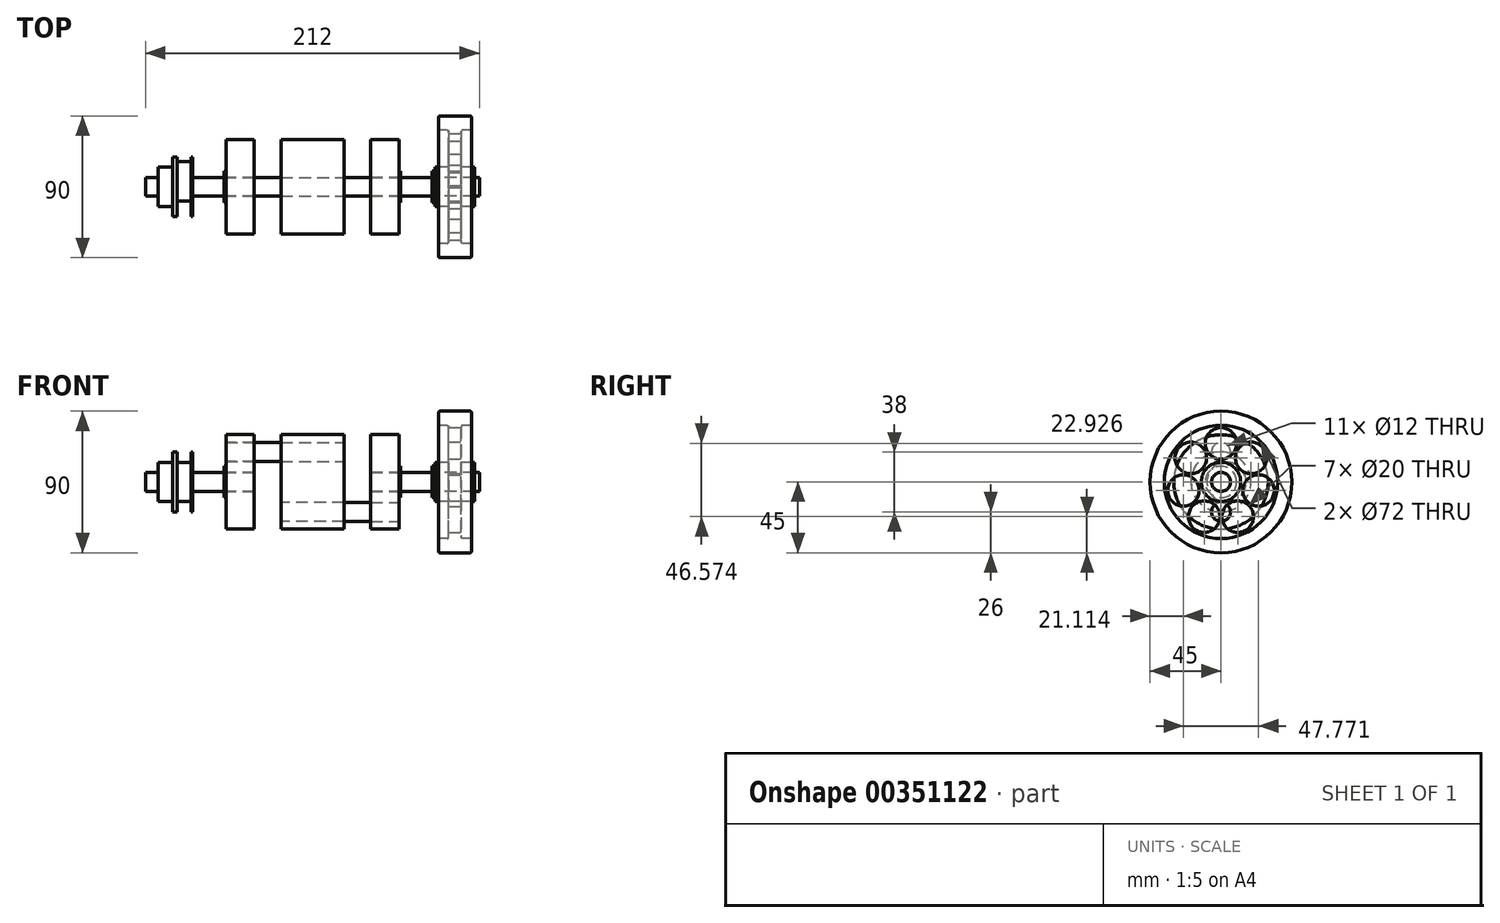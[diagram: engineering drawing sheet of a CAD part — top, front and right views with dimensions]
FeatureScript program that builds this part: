
annotation { "Feature Type Name" : "Feature", "Feature Type Description" : "" }
export const myFeature = defineFeature(function(context is Context, id is Id, definition is map)
    precondition{}
    {
        {
            var Q0;
            Q0=qCreatedBy(makeId("Right.planeOp"),FACE);
            var sketch = newSketch(context, id + "F0", { "sketchPlane" : qUnion([Q0])});
            skCircle(sketch, "E0", {"center": v(0, 0) * mm, "radius": 30 * mm});
            skCircle(sketch, "E1", {"center": v(0, 19) * mm, "radius": 6 * mm});
            skCircle(sketch, "E2", {"center": v(0, -19) * mm, "radius": 6 * mm});
            skSolve(sketch);
        }
        {
            var Q0;
            Q0=makeQuery(id+"F0.imprint","IMPRINT",FACE,{"disambiguationData":[TD([[makeQuery(id+"F0.imprint","IMPRINT",EDGE,{"derivedFrom":sQuery(id+"F0.wireOp",EDGE,"E0")}),1.0]])]});
            extrude(context, id + "F1", {"entities" : qUnion([Q0]), "endBound" : BoundingType.SYMMETRIC, "depth" : 40 * mm});
        }
        {
            var Q0;
            Q0=makeQuery(id+"F0.imprint","IMPRINT",FACE,{"disambiguationData":[TD([[makeQuery(id+"F0.imprint","IMPRINT",EDGE,{"derivedFrom":sQuery(id+"F0.wireOp",EDGE,"E1")}),1.0]])]});
            extrude(context, id + "F2", {"entities" : qUnion([Q0]), "oppositeDirection" : true, "depth" : 55 * mm, "hasSecondDirection" : true, "secondDirectionOppositeDirection" : false, "secondDirectionDepth" : 20 * mm});
        }
        {
            var Q0;
            Q0=makeQuery(id+"F0.imprint","IMPRINT",FACE,{"disambiguationData":[TD([[makeQuery(id+"F0.imprint","IMPRINT",EDGE,{"derivedFrom":sQuery(id+"F0.wireOp",EDGE,"E2")}),1.0]])]});
            extrude(context, id + "F3", {"entities" : qUnion([Q0]), "depth" : 55 * mm, "hasSecondDirection" : true, "secondDirectionOppositeDirection" : true, "secondDirectionDepth" : 20 * mm});
        }
        {
            var Q0;
            Q0=makeQuery(id+"F3.opExtrude","CAP_FACE",FACE,{"disambiguationData":[OSD([sQuery(id+"F0.wireOp",EDGE,"E2")])],"isStart":false});
            var sketch = newSketch(context, id + "F4", { "sketchPlane" : qUnion([Q0])});
            skCircle(sketch, "E3", {"center": v(0, 0) * mm, "radius": 30 * mm});
            skCircle(sketch, "E4", {"center": v(0, 0) * mm, "radius": 6 * mm});
            skCircle(sketch, "E5", {"center": v(0, 0) * mm, "radius": 10 * mm});
            skSolve(sketch);
        }
        {
            var Q0;
            Q0=makeQuery(id+"F4.imprint","IMPRINT",FACE,{"disambiguationData":[TD([[makeQuery(id+"F4.imprint","IMPRINT",EDGE,{"derivedFrom":sQuery(id+"F4.wireOp",EDGE,"E3")}),1.0]])]});
            var Q1;
            Q1=makeQuery(id+"F4.imprint","IMPRINT",FACE,{"disambiguationData":[TD([[makeQuery(id+"F4.imprint","IMPRINT",EDGE,{"derivedFrom":sQuery(id+"F4.wireOp",EDGE,"E4")}),-1.0]])]});
            extrude(context, id + "F5", {"entities" : qUnion([Q0, Q1]), "oppositeDirection" : true, "depth" : 18 * mm});
        }
        {
            var Q0;
            Q0=makeQuery(id+"F5.opExtrude","SWEPT_BODY",BODY,{"disambiguationData":[OSD([sQuery(id+"F0.wireOp",EDGE,"E2"),sQuery(id+"F4.wireOp",EDGE,"E3"),sQuery(id+"F4.wireOp",EDGE,"E4")])]});
            var Q1;
            Q1=qCreatedBy(makeId("Right.planeOp"),FACE);
            mirror(context, id + "F6", {"entities" : qUnion([Q0]), "mirrorPlane" : qUnion([Q1])});
        }
        {
            var Q0;
            Q0=makeQuery(id+"F6.opPattern","COPY",BODY,{"derivedFrom":makeQuery(id+"F5.opExtrude","SWEPT_BODY",BODY,{"disambiguationData":[OSD([sQuery(id+"F0.wireOp",EDGE,"E2"),sQuery(id+"F4.wireOp",EDGE,"E3"),sQuery(id+"F4.wireOp",EDGE,"E4")])]}),"instanceName":"1"});
            var Q1;
            Q1=makeQuery(id+"F6.opPattern","COPY",FACE,{"derivedFrom":makeQuery(id+"F5.opExtrude","SWEPT_FACE",FACE,{"disambiguationData":[OSD([sQuery(id+"F4.wireOp",EDGE,"E4")])]}),"instanceName":"1"});
            transform(context, id + "F7", {"entities" : qUnion([Q0]), "transformType" : TransformType.ROTATION, "transformAxis" : qUnion([Q1]), "angle" : 180 * degree, "makeCopy" : false});
        }
        {
            var Q0;
            Q0=makeQuery(id+"F4.imprint","IMPRINT",FACE,{"disambiguationData":[TD([[makeQuery(id+"F4.imprint","IMPRINT",EDGE,{"derivedFrom":sQuery(id+"F4.wireOp",EDGE,"E4")}),1.0]])]});
            extrude(context, id + "F8", {"entities" : qUnion([Q0]), "depth" : 51 * mm, "hasSecondDirection" : true, "secondDirectionOppositeDirection" : true, "secondDirectionDepth" : 18 * mm});
        }
        {
            var Q0;
            Q0=makeQuery(id+"F4.imprint","IMPRINT",FACE,{"disambiguationData":[TD([[makeQuery(id+"F4.imprint","IMPRINT",EDGE,{"derivedFrom":sQuery(id+"F4.wireOp",EDGE,"E4")}),-1.0]])]});
            extrude(context, id + "F9", {"entities" : qUnion([Q0]), "depth" : 1 * mm});
        }
        {
            var Q0;
            Q0=makeQuery(id+"F8.opExtrude","SWEPT_BODY",BODY,{"disambiguationData":[OSD([sQuery(id+"F4.wireOp",EDGE,"E4")])]});
            var Q1;
            Q1=makeQuery(id+"F9.opExtrude","SWEPT_BODY",BODY,{"disambiguationData":[OSD([sQuery(id+"F4.wireOp",EDGE,"E4"),sQuery(id+"F4.wireOp",EDGE,"E5")])]});
            var Q2;
            Q2=qCreatedBy(makeId("Right.planeOp"),FACE);
            mirror(context, id + "F10", {"entities" : qUnion([Q0, Q1]), "mirrorPlane" : qUnion([Q2])});
        }
        {
            var Q0;
            Q0=qCreatedBy(makeId("Front.planeOp"),FACE);
            var sketch = newSketch(context, id + "F11", { "sketchPlane" : qUnion([Q0])});
            skLineSegment(sketch, "E6", {"start": v(0, 0) * mm, "end": v(137.97, 0) * mm, "construction": true});
            skLineSegment(sketch, "E7", {"start": v(90.5, 52.84) * mm, "end": v(90.5, -56.17) * mm, "construction": true});
            skLineSegment(sketch, "E8", {"start": v(78, -6) * mm, "end": v(103, -6) * mm});
            skLineSegment(sketch, "E9", {"start": v(103, -6) * mm, "end": v(103, -12.5) * mm});
            skLineSegment(sketch, "E10", {"start": v(103, -12.5) * mm, "end": v(94.5, -12.5) * mm});
            skLineSegment(sketch, "E11", {"start": v(94.5, -12.5) * mm, "end": v(94.5, -36) * mm});
            skLineSegment(sketch, "E12", {"start": v(86.5, -36) * mm, "end": v(86.5, -12.5) * mm});
            skLineSegment(sketch, "E13", {"start": v(86.5, -12.5) * mm, "end": v(78, -12.5) * mm});
            skLineSegment(sketch, "E14", {"start": v(78, -12.5) * mm, "end": v(78, -6) * mm});
            skLineSegment(sketch, "E15", {"start": v(94.5, -36) * mm, "end": v(101, -36) * mm});
            skLineSegment(sketch, "E16", {"start": v(101, -36) * mm, "end": v(101, -45) * mm});
            skLineSegment(sketch, "E17", {"start": v(101, -45) * mm, "end": v(80, -45) * mm});
            skLineSegment(sketch, "E18", {"start": v(80, -45) * mm, "end": v(80, -36) * mm});
            skLineSegment(sketch, "E19", {"start": v(80, -36) * mm, "end": v(86.5, -36) * mm});
            skSolve(sketch);
        }
        {
            var Q0;
            Q0=makeQuery(id+"F11.imprint","IMPRINT",FACE,{"disambiguationData":[TD([[makeQuery(id+"F11.imprint","IMPRINT",EDGE,{"derivedFrom":sQuery(id+"F11.wireOp",EDGE,"E8")}),-1.0]])]});
            var Q1;
            Q1=sQuery(id+"F11.wireOp",EDGE,"E6");
            revolve(context, id + "F12", {"entities" : qUnion([Q0]), "axis" : qUnion([Q1]), "revolveType" : RevolveType.FULL});
        }
        {
            var Q0;
            Q0=makeQuery(id+"F12.opRevolve","SWEPT_FACE",FACE,{"disambiguationData":[OSD([sQuery(id+"F11.wireOp",EDGE,"E11")])]});
            var sketch = newSketch(context, id + "F13", { "sketchPlane" : qUnion([Q0])});
            skLineSegment(sketch, "E20", {"start": v(0, 0) * mm, "end": v(0, 49) * mm, "construction": true});
            skCircle(sketch, "E21", {"center": v(0, 24.5) * mm, "radius": 10 * mm});
            skCircle(sketch, "E22.1.0", {"center": v(19.15, 15.28) * mm, "radius": 10 * mm});
            skCircle(sketch, "E22.2.0", {"center": v(23.89, -5.45) * mm, "radius": 10 * mm});
            skCircle(sketch, "E22.3.0", {"center": v(10.63, -22.07) * mm, "radius": 10 * mm});
            skCircle(sketch, "E22.4.0", {"center": v(-10.63, -22.07) * mm, "radius": 10 * mm});
            skCircle(sketch, "E22.5.0", {"center": v(-23.89, -5.45) * mm, "radius": 10 * mm});
            skCircle(sketch, "E22.6.0", {"center": v(-19.15, 15.28) * mm, "radius": 10 * mm});
            skPoint(sketch, "E22.center", {"position": v(0, 0) * mm});
            skLineSegment(sketch, "E22.anchor1", {"start": v(0, 0) * mm, "end": v(0, 24.5) * mm, "construction": true});
            skLineSegment(sketch, "E22.anchor2", {"start": v(0, 0) * mm, "end": v(-19.15, 15.28) * mm, "construction": true});
            skSolve(sketch);
        }
        {
            var Q0;
            Q0=makeQuery(id+"F13.imprint","IMPRINT",FACE,{"disambiguationData":[TD([[makeQuery(id+"F13.imprint","IMPRINT",EDGE,{"derivedFrom":sQuery(id+"F13.wireOp",EDGE,"E22.4.0")}),1.0]])]});
            var Q1;
            Q1=makeQuery(id+"F13.imprint","IMPRINT",FACE,{"disambiguationData":[TD([[makeQuery(id+"F13.imprint","IMPRINT",EDGE,{"derivedFrom":sQuery(id+"F13.wireOp",EDGE,"E22.3.0")}),1.0]])]});
            var Q2;
            Q2=makeQuery(id+"F13.imprint","IMPRINT",FACE,{"disambiguationData":[TD([[makeQuery(id+"F13.imprint","IMPRINT",EDGE,{"derivedFrom":sQuery(id+"F13.wireOp",EDGE,"E22.2.0")}),1.0]])]});
            var Q3;
            Q3=makeQuery(id+"F13.imprint","IMPRINT",FACE,{"disambiguationData":[TD([[makeQuery(id+"F13.imprint","IMPRINT",EDGE,{"derivedFrom":sQuery(id+"F13.wireOp",EDGE,"E22.1.0")}),1.0]])]});
            var Q4;
            Q4=makeQuery(id+"F13.imprint","IMPRINT",FACE,{"disambiguationData":[TD([[makeQuery(id+"F13.imprint","IMPRINT",EDGE,{"derivedFrom":sQuery(id+"F13.wireOp",EDGE,"E21")}),1.0]])]});
            var Q5;
            Q5=makeQuery(id+"F13.imprint","IMPRINT",FACE,{"disambiguationData":[TD([[makeQuery(id+"F13.imprint","IMPRINT",EDGE,{"derivedFrom":sQuery(id+"F13.wireOp",EDGE,"E22.6.0")}),1.0]])]});
            var Q6;
            Q6=makeQuery(id+"F13.imprint","IMPRINT",FACE,{"disambiguationData":[TD([[makeQuery(id+"F13.imprint","IMPRINT",EDGE,{"derivedFrom":sQuery(id+"F13.wireOp",EDGE,"E22.5.0")}),1.0]])]});
            extrude(context, id + "F14", {"entities" : qUnion([Q0, Q1, Q2, Q3, Q4, Q5, Q6]), "operationType" : NewBodyOperationType.REMOVE, "endBound" : BoundingType.UP_TO_NEXT, "oppositeDirection" : true, "depth" : 25 * mm});
        }
        {
            var Q0;
            Q0=makeQuery(id+"F12.opRevolve","SWEPT_EDGE",EDGE,{"disambiguationData":[OSD([sQuery(id+"F11.wireOp",EDGE,"E16"),sQuery(id+"F11.wireOp",EDGE,"E17")])]});
            var Q1;
            Q1=makeQuery(id+"F12.opRevolve","SWEPT_EDGE",EDGE,{"disambiguationData":[OSD([sQuery(id+"F11.wireOp",EDGE,"E15"),sQuery(id+"F11.wireOp",EDGE,"E16")])]});
            var Q2;
            Q2=makeQuery(id+"F12.opRevolve","SWEPT_EDGE",EDGE,{"disambiguationData":[OSD([sQuery(id+"F11.wireOp",EDGE,"E17"),sQuery(id+"F11.wireOp",EDGE,"E18")])]});
            var Q3;
            Q3=makeQuery(id+"F12.opRevolve","SWEPT_EDGE",EDGE,{"disambiguationData":[OSD([sQuery(id+"F11.wireOp",EDGE,"E18"),sQuery(id+"F11.wireOp",EDGE,"E19")])]});
            var Q4;
            Q4=makeQuery(id+"F12.opRevolve","SWEPT_EDGE",EDGE,{"disambiguationData":[OSD([sQuery(id+"F11.wireOp",EDGE,"E11"),sQuery(id+"F11.wireOp",EDGE,"E15")])]});
            var Q5;
            Q5=makeQuery(id+"F12.opRevolve","SWEPT_EDGE",EDGE,{"disambiguationData":[OSD([sQuery(id+"F11.wireOp",EDGE,"E12"),sQuery(id+"F11.wireOp",EDGE,"E19")])]});
            fillet(context, id + "F15", {"entities" : qUnion([Q0, Q1, Q2, Q3, Q4, Q5]), "radius" : 1 * mm, "tangentPropagation" : true, "allowEdgeOverflow" : false});
        }
        {
            var Q0;
            Q0=makeQuery(id+"F9.opExtrude","SWEPT_BODY",BODY,{"disambiguationData":[OSD([sQuery(id+"F4.wireOp",EDGE,"E4"),sQuery(id+"F4.wireOp",EDGE,"E5")])]});
            transform(context, id + "F16", {"entities" : qUnion([Q0]), "transformType" : TransformType.TRANSLATION_3D, "dx" : 21 * mm, "dy" : 0 * mm, "dz" : 0 * mm, "makeCopy" : true});
        }
        {
            var Q0;
            Q0=qCreatedBy(makeId("Right.planeOp"),FACE);
            cPlane(context, id + "F17", {"entities" : qUnion([Q0]), "cplaneType" : CPlaneType.OFFSET, "offset" : 86 * mm, "oppositeDirection" : true, "width" : 150 * mm, "height" : 150 * mm});
        }
        {
            var Q0;
            Q0=qCreatedBy(id+"F17.planeOp",FACE);
            var sketch = newSketch(context, id + "F18", { "sketchPlane" : qUnion([Q0])});
            skCircle(sketch, "E23", {"center": v(0, 0) * mm, "radius": 12.5 * mm});
            skCircle(sketch, "E24", {"center": v(0, 0) * mm, "radius": 6 * mm});
            skCircle(sketch, "E25", {"center": v(0, 0) * mm, "radius": 19 * mm});
            skSolve(sketch);
        }
        {
            var Q0;
            Q0=makeQuery(id+"F18.imprint","IMPRINT",FACE,{"disambiguationData":[TD([[makeQuery(id+"F18.imprint","IMPRINT",EDGE,{"derivedFrom":sQuery(id+"F18.wireOp",EDGE,"E23")}),1.0]])]});
            extrude(context, id + "F19", {"entities" : qUnion([Q0]), "oppositeDirection" : true, "depth" : 12 * mm});
        }
        {
            var Q0;
            Q0=makeQuery(id+"F18.imprint","IMPRINT",FACE,{"disambiguationData":[TD([[makeQuery(id+"F18.imprint","IMPRINT",EDGE,{"derivedFrom":sQuery(id+"F18.wireOp",EDGE,"E23")}),-1.0]])]});
            var Q1;
            Q1=makeQuery(id+"F18.imprint","IMPRINT",FACE,{"disambiguationData":[TD([[makeQuery(id+"F18.imprint","IMPRINT",EDGE,{"derivedFrom":sQuery(id+"F18.wireOp",EDGE,"E23")}),1.0]])]});
            extrude(context, id + "F20", {"entities" : qUnion([Q0, Q1]), "operationType" : NewBodyOperationType.ADD, "oppositeDirection" : true, "depth" : 3 * mm});
        }
        {
            var Q0;
            {var subQ0=sQuery(id+"F18.wireOp",EDGE,"E24");Q0=makeQuery(id+"F20.boolean.opBoolean","MERGE",FACE,{"derivedFrom":[makeQuery(id+"F19.opExtrude","CAP_FACE",FACE,{"disambiguationData":[OSD([sQuery(id+"F18.wireOp",EDGE,"E23"),subQ0])],"isStart":true}),makeQuery(id+"F20.opExtrude","CAP_FACE",FACE,{"disambiguationData":[OSD([subQ0,sQuery(id+"F18.wireOp",EDGE,"E25")])],"isStart":true})]});}
            var sketch = newSketch(context, id + "F21", { "sketchPlane" : qUnion([Q0])});
            skCircle(sketch, "E26", {"center": v(3.5, 0) * mm, "radius": 12.5 * mm});
            skSolve(sketch);
        }
        {
            var Q0;
            Q0=makeQuery(id+"F21.imprint","IMPRINT",FACE,{"disambiguationData":[TD([[makeQuery(id+"F21.imprint","IMPRINT",EDGE,{"derivedFrom":sQuery(id+"F21.wireOp",EDGE,"E26")}),1.0]])]});
            extrude(context, id + "F22", {"entities" : qUnion([Q0]), "operationType" : NewBodyOperationType.ADD, "depth" : 9 * mm});
        }
        {
            var Q0;
            Q0=makeQuery(id+"F22.opExtrude","CAP_FACE",FACE,{"disambiguationData":[OSD([sQuery(id+"F18.wireOp",EDGE,"E24"),sQuery(id+"F21.wireOp",EDGE,"E26")])],"isStart":false});
            var sketch = newSketch(context, id + "F23", { "sketchPlane" : qUnion([Q0])});
            skCircle(sketch, "E27", {"center": v(0, 0) * mm, "radius": 6 * mm});
            skCircle(sketch, "E28", {"center": v(0, 0) * mm, "radius": 19 * mm});
            skSolve(sketch);
        }
        {
            var Q0;
            Q0=makeQuery(id+"F23.imprint","IMPRINT",FACE,{"disambiguationData":[TD([[makeQuery(id+"F23.imprint","IMPRINT",EDGE,{"derivedFrom":sQuery(id+"F23.wireOp",EDGE,"E28")}),1.0]])]});
            var Q1;
            Q1=makeQuery(id+"F23.imprint","IMPRINT",FACE,{"disambiguationData":[TD([[makeQuery(id+"F23.imprint","IMPRINT",EDGE,{"derivedFrom":sQuery(id+"F23.wireOp",EDGE,"E27")}),-1.0]])]});
            extrude(context, id + "F24", {"entities" : qUnion([Q0, Q1]), "depth" : 1 * mm});
        }
    });
